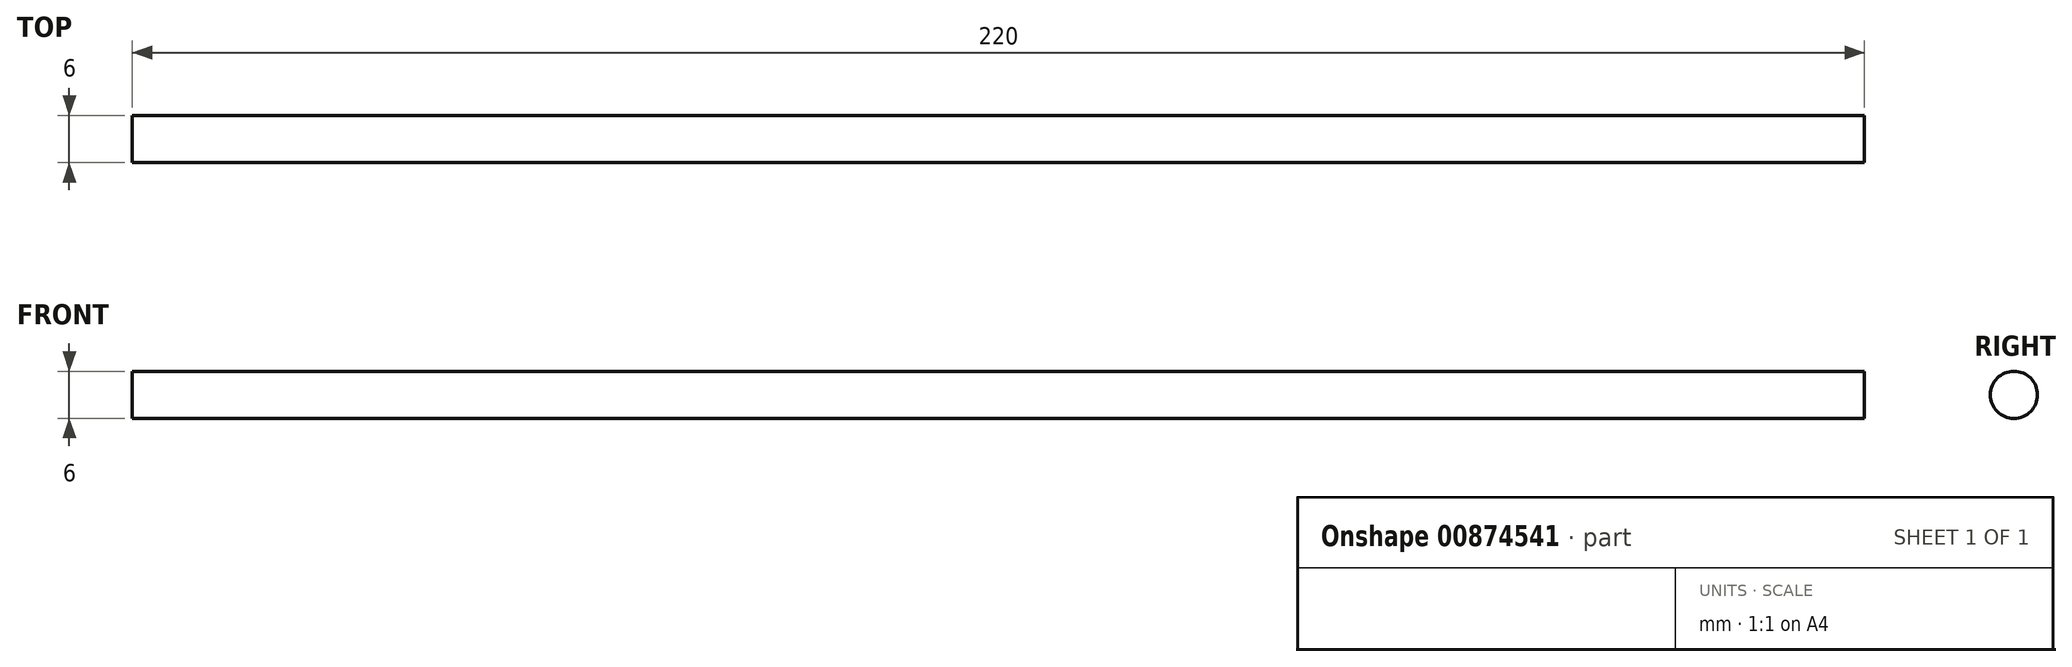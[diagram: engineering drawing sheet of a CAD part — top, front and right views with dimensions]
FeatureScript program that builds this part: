
annotation { "Feature Type Name" : "Feature", "Feature Type Description" : "" }
export const myFeature = defineFeature(function(context is Context, id is Id, definition is map)
    precondition{}
    {
        {
            var Q0;
            Q0=qCreatedBy(makeId("Right.planeOp"),FACE);
            var sketch = newSketch(context, id + "F0", { "sketchPlane" : qUnion([Q0])});
            skCircle(sketch, "E0", {"center": v(0, 0) * mm, "radius": 3 * mm});
            skSolve(sketch);
        }
        {
            var Q0;
            Q0=makeQuery(id+"F0.imprint","IMPRINT",FACE,{"disambiguationData":[TD([[makeQuery(id+"F0.imprint","IMPRINT",EDGE,{"derivedFrom":sQuery(id+"F0.wireOp",EDGE,"E0")}),1.0]])]});
            extrude(context, id + "F1", {"entities" : qUnion([Q0]), "oppositeDirection" : true, "depth" : 220 * mm, "offsetDistance" : 25 * mm});
        }
    });
